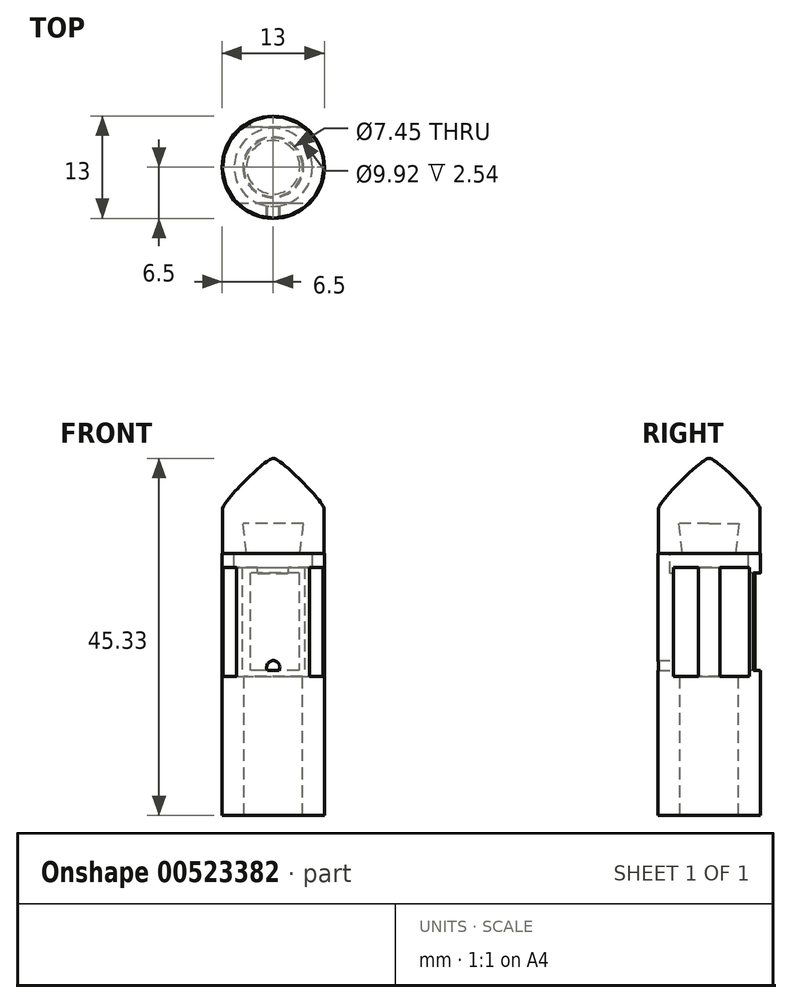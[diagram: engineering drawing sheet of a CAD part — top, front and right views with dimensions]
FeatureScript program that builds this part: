
annotation { "Feature Type Name" : "Feature", "Feature Type Description" : "" }
export const myFeature = defineFeature(function(context is Context, id is Id, definition is map)
    precondition{}
    {
        {
            var Q0;
            Q0=qCreatedBy(makeId("Top.planeOp"),FACE);
            var sketch = newSketch(context, id + "F0", { "sketchPlane" : qUnion([Q0])});
            skCircle(sketch, "E0", {"center": v(0, 0) * mm, "radius": 0.14 * mm});
            skCircle(sketch, "E1", {"center": v(0, 0) * mm, "radius": 6.5 * mm});
            skSolve(sketch);
        }
        {
            var Q0;
            Q0=makeQuery(id+"F0.imprint","IMPRINT",FACE,{"disambiguationData":[TD([[makeQuery(id+"F0.imprint","IMPRINT",EDGE,{"derivedFrom":sQuery(id+"F0.wireOp",EDGE,"E0")}),-1.0]])]});
            extrude(context, id + "F1", {"entities" : qUnion([Q0]), "endBound" : BoundingType.SYMMETRIC, "depth" : 33.28 * mm, "offsetDistance" : 25.4 * mm});
        }
        {
            var Q0;
            Q0=qCreatedBy(makeId("Right.planeOp"),FACE);
            var sketch = newSketch(context, id + "F2", { "sketchPlane" : qUnion([Q0])});
            skLineSegment(sketch, "E2.bottom", {"start": v(-4.55, 14.89) * mm, "end": v(5.13, 14.89) * mm});
            skLineSegment(sketch, "E2.top", {"start": v(-4.55, 1) * mm, "end": v(5.13, 1) * mm});
            skLineSegment(sketch, "E2.left", {"start": v(-4.55, 14.89) * mm, "end": v(-4.55, 1) * mm});
            skLineSegment(sketch, "E2.right", {"start": v(5.13, 14.89) * mm, "end": v(5.13, 1) * mm});
            skSolve(sketch);
        }
        {
            var Q0;
            Q0 = qSketchRegion(id + "F2", true);
            var Q1;
            Q1 = qSketchRegion(id + "F2", true);
            extrude(context, id + "F3", {"entities" : qUnion([Q0]), "operationType" : NewBodyOperationType.REMOVE, "surfaceEntities" : qUnion([Q1]), "endBound" : BoundingType.SYMMETRIC, "oppositeDirection" : true, "depth" : 12.7 * mm, "offsetDistance" : 25.4 * mm});
        }
        {
            var Q0;
            Q0=makeQuery(id+"F3.boolean.opBoolean","COPY",FACE,{"derivedFrom":makeQuery(id+"F3.opExtrude","SWEPT_FACE",FACE,{"disambiguationData":[OSD([sQuery(id+"F2.wireOp",EDGE,"E2.left")])]})});
            var sketch = newSketch(context, id + "F4", { "sketchPlane" : qUnion([Q0])});
            skLineSegment(sketch, "E3.bottom", {"start": v(-3.27, 14.14) * mm, "end": v(2.95, 14.14) * mm});
            skLineSegment(sketch, "E3.top", {"start": v(-3.27, 1.77) * mm, "end": v(2.95, 1.77) * mm});
            skLineSegment(sketch, "E3.left", {"start": v(-3.27, 14.14) * mm, "end": v(-3.27, 1.77) * mm});
            skLineSegment(sketch, "E3.right", {"start": v(2.95, 14.14) * mm, "end": v(2.95, 1.77) * mm});
            skSolve(sketch);
        }
        {
            var Q0;
            Q0 = qSketchRegion(id + "F4", true);
            var sketch = newSketch(context, id + "F5", { "sketchPlane" : qUnion([Q0])});
            skSolve(sketch);
        }
        {
            var Q0;
            Q0 = qSketchRegion(id + "F5", true);
            var Q1;
            Q1=makeQuery(id+"F4.imprint","IMPRINT",FACE,{"disambiguationData":[TD([[makeQuery(id+"F4.imprint","IMPRINT",EDGE,{"derivedFrom":sQuery(id+"F4.wireOp",EDGE,"E3.bottom")}),-1.0]])]});
            extrude(context, id + "F6", {"entities" : qUnion([Q0, Q1]), "operationType" : NewBodyOperationType.REMOVE, "endBound" : BoundingType.THROUGH_ALL, "depth" : 25.4 * mm, "offsetDistance" : 25.4 * mm});
        }
        {
            var Q0;
            Q0=makeQuery(id+"F3.boolean.opBoolean","COPY",FACE,{"derivedFrom":makeQuery(id+"F3.opExtrude","SWEPT_FACE",FACE,{"disambiguationData":[OSD([sQuery(id+"F2.wireOp",EDGE,"E2.top")])]})});
            var sketch = newSketch(context, id + "F7", { "sketchPlane" : qUnion([Q0])});
            skCircle(sketch, "E4", {"center": v(0, 0) * mm, "radius": 3.73 * mm});
            skSolve(sketch);
        }
        {
            var Q0;
            Q0=makeQuery(id+"F7.imprint","IMPRINT",FACE,{"disambiguationData":[TD([[makeQuery(id+"F7.imprint","IMPRINT",EDGE,{"derivedFrom":sQuery(id+"F7.wireOp",EDGE,"E4")}),1.0]])]});
            extrude(context, id + "F8", {"entities" : qUnion([Q0]), "operationType" : NewBodyOperationType.REMOVE, "oppositeDirection" : true, "depth" : 25.4 * mm, "offsetDistance" : 25.4 * mm});
        }
        {
            var Q0;
            Q0=makeQuery(id+"F5.imprint","IMPRINT",FACE,{"disambiguationData":[TD([[makeQuery(id+"F5.imprint","IMPRINT",EDGE,{"derivedFrom":makeQuery(id+"F4.imprint","IMPRINT",EDGE,{"derivedFrom":sQuery(id+"F4.wireOp",EDGE,"E3.bottom")})}),-1.0]])]});
            var sketch = newSketch(context, id + "F9", { "sketchPlane" : qUnion([Q0])});
            skCircle(sketch, "E5", {"center": v(0, 2.18) * mm, "radius": 0.84 * mm});
            skSolve(sketch);
        }
        {
            var Q0;
            {var subQ0=sQuery(id+"F9.wireOp",EDGE,"E5");var subQ1=makeQuery(id+"F5.imprint","IMPRINT",EDGE,{"derivedFrom":makeQuery(id+"F4.imprint","IMPRINT",EDGE,{"derivedFrom":sQuery(id+"F4.wireOp",EDGE,"E3.top")})});var subQ2=makeQuery(id+"F9.imprint","INTERSECT",VERTEX,{"disambiguationData":[OD(0.0)],"derivedFrom":[subQ1,subQ0]});Q0=makeQuery(id+"F9.imprint","IMPRINT",FACE,{"disambiguationData":[TD([[makeQuery(id+"F9.imprint","IMPRINT",EDGE,{"disambiguationData":[TD([[subQ2,1.0]])],"derivedFrom":subQ0}),1.0]])]});}
            var Q1;
            Q1=sQuery(id+"F9.wireOp",EDGE,"E5");
            extrude(context, id + "F10", {"entities" : qUnion([Q0]), "operationType" : NewBodyOperationType.REMOVE, "surfaceEntities" : qUnion([Q1]), "endBound" : BoundingType.SYMMETRIC, "oppositeDirection" : true, "depth" : 25.4 * mm, "offsetDistance" : 25.4 * mm});
        }
        {
            var Q0;
            Q0=makeQuery(id+"F1.opExtrude","CAP_FACE",FACE,{"disambiguationData":[OSD([sQuery(id+"F0.wireOp",EDGE,"E0"),sQuery(id+"F0.wireOp",EDGE,"E1")])],"isStart":false});
            var sketch = newSketch(context, id + "F11", { "sketchPlane" : qUnion([Q0])});
            skCircle(sketch, "E6", {"center": v(0, 0) * mm, "radius": 4.96 * mm});
            skSolve(sketch);
        }
        {
            var Q0;
            Q0=makeQuery(id+"F11.imprint","IMPRINT",FACE,{"disambiguationData":[TD([[makeQuery(id+"F11.imprint","IMPRINT",EDGE,{"derivedFrom":sQuery(id+"F11.wireOp",EDGE,"E6")}),1.0]])]});
            var Q1;
            Q1=sQuery(id+"F11.wireOp",EDGE,"E6");
            extrude(context, id + "F12", {"entities" : qUnion([Q0]), "operationType" : NewBodyOperationType.REMOVE, "surfaceEntities" : qUnion([Q1]), "endBound" : BoundingType.SYMMETRIC, "oppositeDirection" : true, "depth" : 5.08 * mm, "offsetDistance" : 25.4 * mm});
        }
        {
            var Q0;
            Q0=makeQuery(id+"F1.opExtrude","CAP_FACE",FACE,{"disambiguationData":[OSD([sQuery(id+"F0.wireOp",EDGE,"E0"),sQuery(id+"F0.wireOp",EDGE,"E1")])],"isStart":false});
            var sketch = newSketch(context, id + "F13", { "sketchPlane" : qUnion([Q0])});
            skCircle(sketch, "E7", {"center": v(0, 0) * mm, "radius": 6.45 * mm});
            skSolve(sketch);
        }
        {
            var Q0;
            Q0 = qSketchRegion(id + "F13", true);
            extrude(context, id + "F14", {"entities" : qUnion([Q0]), "operationType" : NewBodyOperationType.ADD, "depth" : 12.06 * mm, "offsetDistance" : 25.4 * mm});
        }
        {
            var Q0;
            Q0=makeQuery(id+"F14.opExtrude","CAP_EDGE",EDGE,{"disambiguationData":[OSD([sQuery(id+"F13.wireOp",EDGE,"E7")])],"isStart":false});
            fillet(context, id + "F15", {"entities" : qUnion([Q0]), "radius" : 6.35 * mm, "tangentPropagation" : true, "rho" : 0.1, "crossSection" : FilletCrossSection.CONIC, "allowEdgeOverflow" : false});
        }
        {
            var Q0;
            Q0=makeQuery(id+"F14.opExtrude","CAP_FACE",FACE,{"disambiguationData":[OSD([sQuery(id+"F13.wireOp",EDGE,"E7")])],"isStart":true});
            var sketch = newSketch(context, id + "F16", { "sketchPlane" : qUnion([Q0])});
            skCircle(sketch, "E8", {"center": v(0, 0) * mm, "radius": 3.39 * mm});
            skSolve(sketch);
        }
        {
            var Q0;
            Q0 = qSketchRegion(id + "F16", true);
            extrude(context, id + "F17", {"entities" : qUnion([Q0]), "operationType" : NewBodyOperationType.REMOVE, "endBound" : BoundingType.SYMMETRIC, "oppositeDirection" : true, "depth" : 7.62 * mm, "offsetDistance" : 25.4 * mm, "hasDraft" : true, "draftAngle" : 7 * degree});
        }
    });
